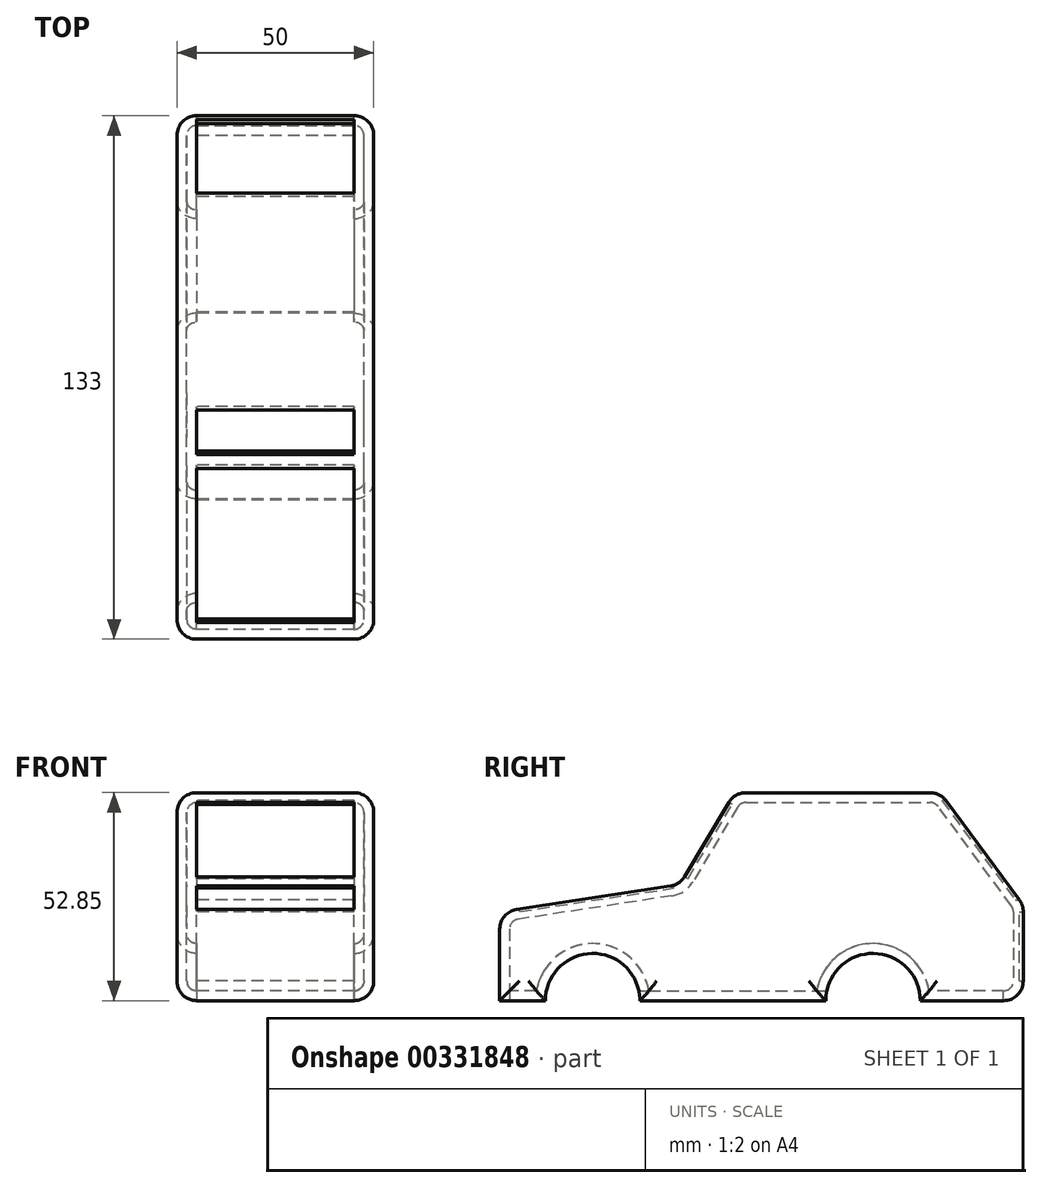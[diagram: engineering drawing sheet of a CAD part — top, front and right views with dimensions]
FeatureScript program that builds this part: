
annotation { "Feature Type Name" : "Feature", "Feature Type Description" : "" }
export const myFeature = defineFeature(function(context is Context, id is Id, definition is map)
    precondition{}
    {
        {
            var Q0;
            Q0=qCreatedBy(makeId("Right.planeOp"),FACE);
            var sketch = newSketch(context, id + "F0", { "sketchPlane" : qUnion([Q0])});
            skLineSegment(sketch, "E0.bottom", {"start": v(-62.62, 0) * mm, "end": v(70.38, 0) * mm});
            skLineSegment(sketch, "E0.top", {"start": v(-62.62, 52.85) * mm, "end": v(70.38, 52.85) * mm});
            skLineSegment(sketch, "E0.left", {"start": v(-62.62, 0) * mm, "end": v(-62.62, 52.85) * mm});
            skLineSegment(sketch, "E0.right", {"start": v(70.38, 0) * mm, "end": v(70.38, 52.85) * mm});
            skCircle(sketch, "E1", {"center": v(32.2, 0) * mm, "radius": 12 * mm});
            skCircle(sketch, "E2", {"center": v(-39.01, 0) * mm, "radius": 12 * mm});
            skLineSegment(sketch, "E3", {"start": v(-62.62, 22.5) * mm, "end": v(-16.87, 29.48) * mm});
            skLineSegment(sketch, "E4", {"start": v(-16.87, 29.48) * mm, "end": v(-2.9, 52.85) * mm});
            skLineSegment(sketch, "E5", {"start": v(-2.9, 52.85) * mm, "end": v(49.27, 52.85) * mm});
            skLineSegment(sketch, "E6", {"start": v(49.27, 52.85) * mm, "end": v(70.38, 24.25) * mm});
            skSolve(sketch);
        }
        {
            var Q0;
            {var subQ12=sQuery(id+"F0.wireOp",EDGE,"E3");Q0=makeQuery(id+"F0.imprint","IMPRINT",FACE,{"disambiguationData":[TD([[makeQuery(id+"F0.imprint","IMPRINT",EDGE,{"derivedFrom":subQ12}),-1.0]])]});}
            extrude(context, id + "F1", {"entities" : qUnion([Q0]), "depth" : 25 * mm});
        }
        {
            var Q0;
            Q0=makeQuery(id+"F1.opExtrude","CAP_FACE",FACE,{"disambiguationData":[OSD([sQuery(id+"F0.wireOp",EDGE,"E0.bottom"),sQuery(id+"F0.wireOp",EDGE,"E0.left"),sQuery(id+"F0.wireOp",EDGE,"E0.right"),sQuery(id+"F0.wireOp",EDGE,"E1"),sQuery(id+"F0.wireOp",EDGE,"E2"),sQuery(id+"F0.wireOp",EDGE,"E3"),sQuery(id+"F0.wireOp",EDGE,"E4"),sQuery(id+"F0.wireOp",EDGE,"E5"),sQuery(id+"F0.wireOp",EDGE,"E6")])],"isStart":true});
            extrude(context, id + "F2", {"entities" : qUnion([Q0]), "operationType" : NewBodyOperationType.ADD, "depth" : 25 * mm});
        }
        {
            var Q0;
            {var subQ0=sQuery(id+"F0.wireOp",EDGE,"E6");var subQ1=sQuery(id+"F0.wireOp",EDGE,"E5");var subQ2=sQuery(id+"F0.wireOp",EDGE,"E0.top");Q0=makeQuery(id+"F2.boolean.opBoolean","MERGE",EDGE,{"derivedFrom":[makeQuery(id+"F1.opExtrude","SWEPT_EDGE",EDGE,{"disambiguationData":[OSD([subQ2,subQ1,subQ0])]}),makeQuery(id+"F2.opExtrude","SWEPT_EDGE",EDGE,{"disambiguationData":[OSD([subQ2,subQ1,subQ0])]})]});}
            var Q1;
            Q1=makeQuery(id+"F1.opExtrude","CAP_EDGE",EDGE,{"disambiguationData":[OSD([sQuery(id+"F0.wireOp",EDGE,"E0.right")])],"isStart":false});
            var Q2;
            Q2=makeQuery(id+"F1.opExtrude","CAP_FACE",FACE,{"disambiguationData":[OSD([sQuery(id+"F0.wireOp",EDGE,"E0.bottom"),sQuery(id+"F0.wireOp",EDGE,"E0.left"),sQuery(id+"F0.wireOp",EDGE,"E0.right"),sQuery(id+"F0.wireOp",EDGE,"E1"),sQuery(id+"F0.wireOp",EDGE,"E2"),sQuery(id+"F0.wireOp",EDGE,"E3"),sQuery(id+"F0.wireOp",EDGE,"E4"),sQuery(id+"F0.wireOp",EDGE,"E5"),sQuery(id+"F0.wireOp",EDGE,"E6")])],"isStart":false});
            var Q3;
            {var subQ0=sQuery(id+"F0.wireOp",EDGE,"E3");Q3=makeQuery(id+"F2.boolean.opBoolean","MERGE",FACE,{"derivedFrom":[makeQuery(id+"F1.opExtrude","SWEPT_FACE",FACE,{"disambiguationData":[OSD([subQ0])]}),makeQuery(id+"F2.opExtrude","SWEPT_FACE",FACE,{"disambiguationData":[OSD([subQ0])]})]});}
            var Q4;
            {var subQ0=sQuery(id+"F0.wireOp",EDGE,"E4");Q4=makeQuery(id+"F2.boolean.opBoolean","MERGE",FACE,{"derivedFrom":[makeQuery(id+"F1.opExtrude","SWEPT_FACE",FACE,{"disambiguationData":[OSD([subQ0])]}),makeQuery(id+"F2.opExtrude","SWEPT_FACE",FACE,{"disambiguationData":[OSD([subQ0])]})]});}
            var Q5;
            Q5=makeQuery(id+"F2.opExtrude","CAP_FACE",FACE,{"disambiguationData":[OSD([sQuery(id+"F0.wireOp",EDGE,"E0.bottom"),sQuery(id+"F0.wireOp",EDGE,"E0.left"),sQuery(id+"F0.wireOp",EDGE,"E0.right"),sQuery(id+"F0.wireOp",EDGE,"E1"),sQuery(id+"F0.wireOp",EDGE,"E2"),sQuery(id+"F0.wireOp",EDGE,"E3"),sQuery(id+"F0.wireOp",EDGE,"E4"),sQuery(id+"F0.wireOp",EDGE,"E5"),sQuery(id+"F0.wireOp",EDGE,"E6")])],"isStart":false});
            var Q6;
            {var subQ0=sQuery(id+"F0.wireOp",EDGE,"E0.right");Q6=makeQuery(id+"F2.boolean.opBoolean","MERGE",FACE,{"derivedFrom":[makeQuery(id+"F1.opExtrude","SWEPT_FACE",FACE,{"disambiguationData":[OSD([subQ0])]}),makeQuery(id+"F2.opExtrude","SWEPT_FACE",FACE,{"disambiguationData":[OSD([subQ0])]})]});}
            var Q7;
            {var subQ0=sQuery(id+"F0.wireOp",EDGE,"E6");Q7=makeQuery(id+"F2.boolean.opBoolean","MERGE",FACE,{"derivedFrom":[makeQuery(id+"F1.opExtrude","SWEPT_FACE",FACE,{"disambiguationData":[OSD([subQ0])]}),makeQuery(id+"F2.opExtrude","SWEPT_FACE",FACE,{"disambiguationData":[OSD([subQ0])]})]});}
            fillet(context, id + "F3", {"entities" : qUnion([Q0, Q1, Q2, Q3, Q4, Q5, Q6, Q7]), "radius" : 5 * mm, "tangentPropagation" : true, "allowEdgeOverflow" : false});
        }
        {
            var Q0;
            {var subQ0=sQuery(id+"F0.wireOp",EDGE,"E0.bottom");var subQ1=makeQuery(id+"F0.imprint","IMPRINT",EDGE,{"disambiguationData":[TD([[makeQuery(id+"F0.imprint","INTERSECT",VERTEX,{"disambiguationData":[OD(1.0)],"derivedFrom":[subQ0,sQuery(id+"F0.wireOp",EDGE,"E2")]}),-1.0]])],"derivedFrom":subQ0});Q0=makeQuery(id+"F2.boolean.opBoolean","MERGE",FACE,{"derivedFrom":[makeQuery(id+"F1.opExtrude","SWEPT_FACE",FACE,{"disambiguationData":[OSD([subQ0]),TDD([subQ1])]}),makeQuery(id+"F2.opExtrude","SWEPT_FACE",FACE,{"disambiguationData":[OSD([subQ0]),TDD([makeQuery(id+"F1.opExtrude","CAP_EDGE",EDGE,{"disambiguationData":[OSD([subQ0]),TDD([subQ1])],"isStart":true})])]})]});}
            var Q1;
            {var subQ0=sQuery(id+"F0.wireOp",EDGE,"E2");Q1=makeQuery(id+"F2.boolean.opBoolean","MERGE",FACE,{"derivedFrom":[makeQuery(id+"F1.opExtrude","SWEPT_FACE",FACE,{"disambiguationData":[OSD([subQ0])]}),makeQuery(id+"F2.opExtrude","SWEPT_FACE",FACE,{"disambiguationData":[OSD([subQ0])]})]});}
            var Q2;
            {var subQ0=sQuery(id+"F0.wireOp",EDGE,"E1");Q2=makeQuery(id+"F2.boolean.opBoolean","MERGE",FACE,{"derivedFrom":[makeQuery(id+"F1.opExtrude","SWEPT_FACE",FACE,{"disambiguationData":[OSD([subQ0])]}),makeQuery(id+"F2.opExtrude","SWEPT_FACE",FACE,{"disambiguationData":[OSD([subQ0])]})]});}
            var Q3;
            {var subQ0=sQuery(id+"F0.wireOp",EDGE,"E0.bottom");var subQ1=makeQuery(id+"F0.imprint","IMPRINT",EDGE,{"disambiguationData":[TD([[makeQuery(id+"F0.imprint","INTERSECT",VERTEX,{"derivedFrom":[subQ0,sQuery(id+"F0.wireOp",EDGE,"E0.left")]}),-1.0]])],"derivedFrom":subQ0});Q3=makeQuery(id+"F2.boolean.opBoolean","MERGE",FACE,{"derivedFrom":[makeQuery(id+"F1.opExtrude","SWEPT_FACE",FACE,{"disambiguationData":[OSD([subQ0]),TDD([subQ1])]}),makeQuery(id+"F2.opExtrude","SWEPT_FACE",FACE,{"disambiguationData":[OSD([subQ0]),TDD([makeQuery(id+"F1.opExtrude","CAP_EDGE",EDGE,{"disambiguationData":[OSD([subQ0]),TDD([subQ1])],"isStart":true})])]})]});}
            var Q4;
            {var subQ0=sQuery(id+"F0.wireOp",EDGE,"E0.bottom");var subQ1=makeQuery(id+"F0.imprint","IMPRINT",EDGE,{"disambiguationData":[TD([[makeQuery(id+"F0.imprint","INTERSECT",VERTEX,{"derivedFrom":[subQ0,sQuery(id+"F0.wireOp",EDGE,"E0.right")]}),1.0]])],"derivedFrom":subQ0});Q4=makeQuery(id+"F2.boolean.opBoolean","MERGE",FACE,{"derivedFrom":[makeQuery(id+"F1.opExtrude","SWEPT_FACE",FACE,{"disambiguationData":[OSD([subQ0]),TDD([subQ1])]}),makeQuery(id+"F2.opExtrude","SWEPT_FACE",FACE,{"disambiguationData":[OSD([subQ0]),TDD([makeQuery(id+"F1.opExtrude","CAP_EDGE",EDGE,{"disambiguationData":[OSD([subQ0]),TDD([subQ1])],"isStart":true})])]})]});}
            shell(context, id + "F4", {"entities" : qUnion([Q0, Q1, Q2, Q3, Q4]), "thickness" : 2.5 * mm});
        }
        {
            var Q0;
            {var subQ0=sQuery(id+"F0.wireOp",EDGE,"E4");Q0=makeQuery(id+"F2.boolean.opBoolean","MERGE",FACE,{"derivedFrom":[makeQuery(id+"F1.opExtrude","SWEPT_FACE",FACE,{"disambiguationData":[OSD([subQ0])]}),makeQuery(id+"F2.opExtrude","SWEPT_FACE",FACE,{"disambiguationData":[OSD([subQ0])]})]});}
            var Q1;
            {var subQ0=sQuery(id+"F0.wireOp",EDGE,"E3");Q1=makeQuery(id+"F2.boolean.opBoolean","MERGE",FACE,{"derivedFrom":[makeQuery(id+"F1.opExtrude","SWEPT_FACE",FACE,{"disambiguationData":[OSD([subQ0])]}),makeQuery(id+"F2.opExtrude","SWEPT_FACE",FACE,{"disambiguationData":[OSD([subQ0])]})]});}
            extrude(context, id + "F5", {"entities" : qUnion([Q0, Q1]), "operationType" : NewBodyOperationType.REMOVE, "oppositeDirection" : true, "depth" : 1 * mm});
        }
        {
            var Q0;
            {var subQ0=sQuery(id+"F0.wireOp",EDGE,"E0.right");Q0=makeQuery(id+"F2.boolean.opBoolean","MERGE",FACE,{"derivedFrom":[makeQuery(id+"F1.opExtrude","SWEPT_FACE",FACE,{"disambiguationData":[OSD([subQ0])]}),makeQuery(id+"F2.opExtrude","SWEPT_FACE",FACE,{"disambiguationData":[OSD([subQ0])]})]});}
            var Q1;
            {var subQ0=sQuery(id+"F0.wireOp",EDGE,"E6");Q1=makeQuery(id+"F2.boolean.opBoolean","MERGE",FACE,{"derivedFrom":[makeQuery(id+"F1.opExtrude","SWEPT_FACE",FACE,{"disambiguationData":[OSD([subQ0])]}),makeQuery(id+"F2.opExtrude","SWEPT_FACE",FACE,{"disambiguationData":[OSD([subQ0])]})]});}
            extrude(context, id + "F6", {"entities" : qUnion([Q0, Q1]), "operationType" : NewBodyOperationType.REMOVE, "oppositeDirection" : true, "depth" : 1 * mm});
        }
    });
